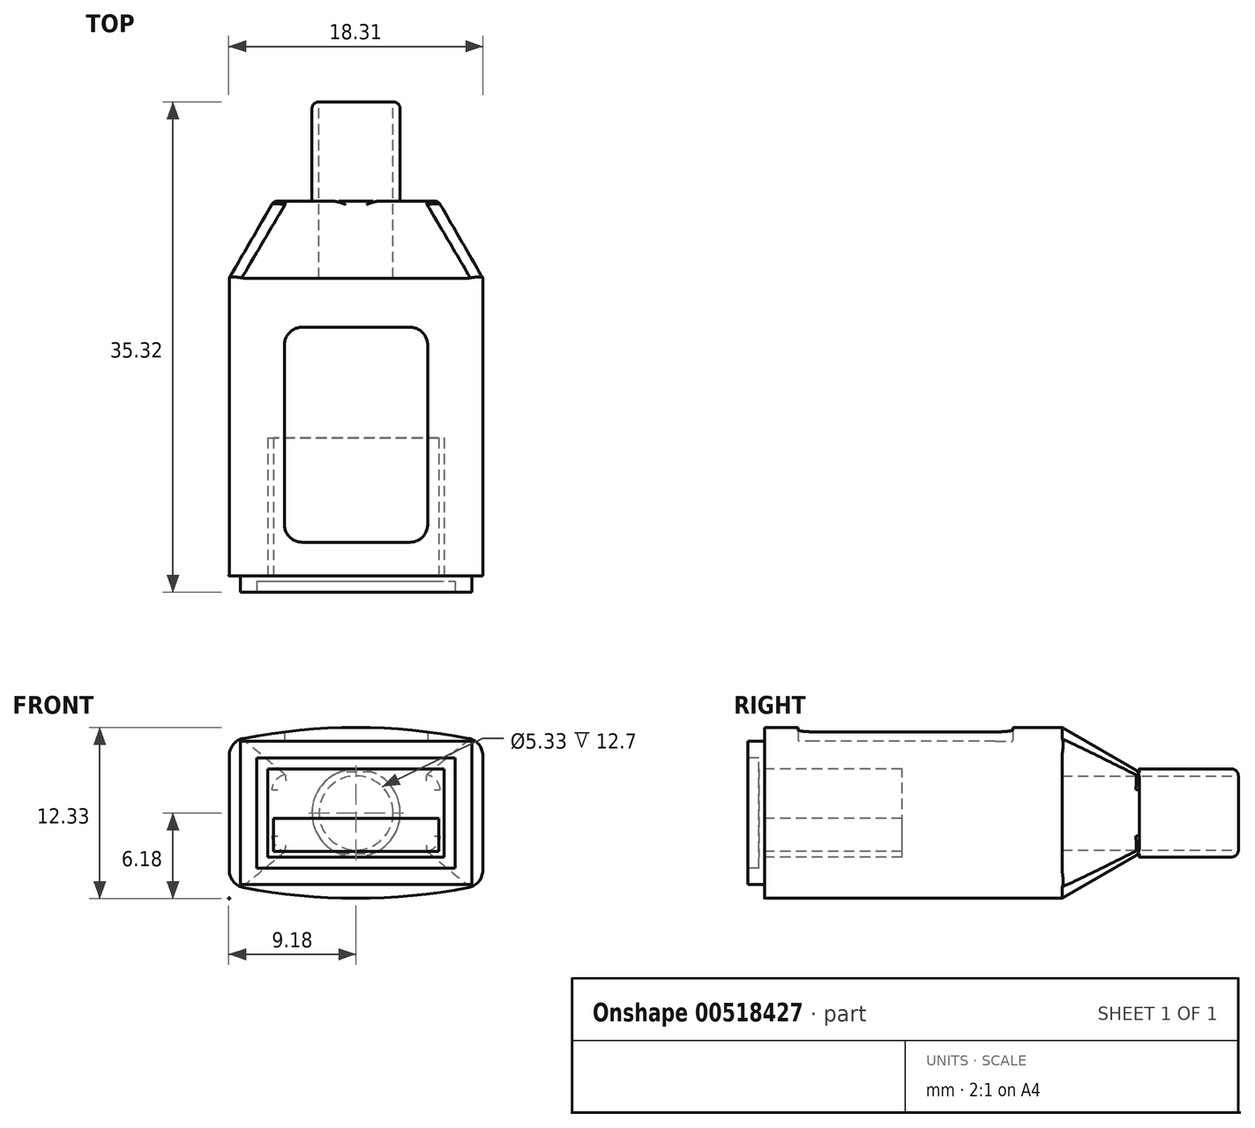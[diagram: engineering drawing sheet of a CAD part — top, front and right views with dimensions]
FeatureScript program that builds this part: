
annotation { "Feature Type Name" : "Feature", "Feature Type Description" : "" }
export const myFeature = defineFeature(function(context is Context, id is Id, definition is map)
    precondition{}
    {
        {
            var Q0;
            Q0=qCreatedBy(makeId("Front.planeOp"),FACE);
            var sketch = newSketch(context, id + "F0", { "sketchPlane" : qUnion([Q0])});
            skLineSegment(sketch, "E0.left", {"start": v(9.13, 0) * mm, "end": v(9.13, 5.16) * mm});
            skLineSegment(sketch, "E0.right", {"start": v(-9.13, 0) * mm, "end": v(-9.13, 5.16) * mm});
            skPoint(sketch, "E0.middle", {"position": v(0, 0) * mm});
            skArc(sketch, "E1", {"start": v(9.13, 5.16) * mm, "mid": v(0, 6.15) * mm, "end": v(-9.13, 5.16) * mm});
            skLineSegment(sketch, "E2", {"start": v(-9.13, 0) * mm, "end": v(9.13, 0) * mm, "construction": true});
            skArc(sketch, "E3.MirrorCS", {"start": v(9.13, -5.16) * mm, "mid": v(0, -6.15) * mm, "end": v(-9.13, -5.16) * mm});
            skLineSegment(sketch, "E4.MirrorCS", {"start": v(-9.13, 0) * mm, "end": v(-9.13, -5.16) * mm});
            skLineSegment(sketch, "E5.MirrorCS", {"start": v(9.13, 0) * mm, "end": v(9.13, -5.16) * mm});
            skSolve(sketch);
        }
        {
            var Q0;
            Q0 = qSketchRegion(id + "F0", true);
            extrude(context, id + "F1", {"entities" : qUnion([Q0]), "depth" : 21.43 * mm, "offsetDistance" : 25.4 * mm});
        }
        {
            var Q0;
            Q0=makeQuery(id+"F1.opExtrude","CAP_FACE",FACE,{"disambiguationData":[OSD([sQuery(id+"F0.wireOp",EDGE,"E0.left"),sQuery(id+"F0.wireOp",EDGE,"E0.right"),sQuery(id+"F0.wireOp",EDGE,"E1"),sQuery(id+"F0.wireOp",EDGE,"E3.MirrorCS"),sQuery(id+"F0.wireOp",EDGE,"E4.MirrorCS"),sQuery(id+"F0.wireOp",EDGE,"E5.MirrorCS")])],"isStart":false});
            var sketch = newSketch(context, id + "F2", { "sketchPlane" : qUnion([Q0])});
            skLineSegment(sketch, "E6.bottom", {"start": v(8.33, -5.16) * mm, "end": v(-8.33, -5.16) * mm});
            skLineSegment(sketch, "E6.top", {"start": v(8.33, 5.16) * mm, "end": v(-8.33, 5.16) * mm});
            skLineSegment(sketch, "E6.left", {"start": v(8.33, -5.16) * mm, "end": v(8.33, 5.16) * mm});
            skLineSegment(sketch, "E6.right", {"start": v(-8.33, -5.16) * mm, "end": v(-8.33, 5.16) * mm});
            skPoint(sketch, "E6.middle", {"position": v(0, 0) * mm});
            skSolve(sketch);
        }
        {
            var Q0;
            Q0 = qSketchRegion(id + "F2", true);
            extrude(context, id + "F3", {"entities" : qUnion([Q0]), "operationType" : NewBodyOperationType.ADD, "depth" : 1.2 * mm, "offsetDistance" : 25.4 * mm});
        }
        {
            var Q0;
            Q0=makeQuery(id+"F3.opExtrude","CAP_FACE",FACE,{"disambiguationData":[OSD([sQuery(id+"F2.wireOp",EDGE,"E6.bottom"),sQuery(id+"F2.wireOp",EDGE,"E6.top"),sQuery(id+"F2.wireOp",EDGE,"E6.left"),sQuery(id+"F2.wireOp",EDGE,"E6.right")])],"isStart":false});
            var sketch = newSketch(context, id + "F4", { "sketchPlane" : qUnion([Q0])});
            skLineSegment(sketch, "E7.0", {"start": v(7.14, -3.97) * mm, "end": v(7.14, 3.97) * mm});
            skLineSegment(sketch, "E7.1", {"start": v(-7.14, -3.97) * mm, "end": v(7.14, -3.97) * mm});
            skLineSegment(sketch, "E7.2", {"start": v(-7.14, 3.97) * mm, "end": v(-7.14, -3.97) * mm});
            skLineSegment(sketch, "E7.3", {"start": v(7.14, 3.97) * mm, "end": v(-7.14, 3.97) * mm});
            skSolve(sketch);
        }
        {
            var Q0;
            Q0 = qSketchRegion(id + "F4", true);
            extrude(context, id + "F5", {"entities" : qUnion([Q0]), "operationType" : NewBodyOperationType.REMOVE, "oppositeDirection" : true, "depth" : 0.8 * mm, "offsetDistance" : 25.4 * mm});
        }
        {
            var Q0;
            Q0=makeQuery(id+"F5.boolean.opBoolean","COPY",FACE,{"derivedFrom":makeQuery(id+"F5.opExtrude","CAP_FACE",FACE,{"disambiguationData":[OSD([sQuery(id+"F4.wireOp",EDGE,"E7.0"),sQuery(id+"F4.wireOp",EDGE,"E7.1"),sQuery(id+"F4.wireOp",EDGE,"E7.2"),sQuery(id+"F4.wireOp",EDGE,"E7.3")])],"isStart":false})});
            var sketch = newSketch(context, id + "F6", { "sketchPlane" : qUnion([Q0])});
            skLineSegment(sketch, "E8.0", {"start": v(6.35, -3.18) * mm, "end": v(6.35, 3.18) * mm});
            skLineSegment(sketch, "E8.1", {"start": v(-6.35, -3.18) * mm, "end": v(6.35, -3.18) * mm});
            skLineSegment(sketch, "E8.2", {"start": v(-6.35, 3.18) * mm, "end": v(-6.35, -3.18) * mm});
            skLineSegment(sketch, "E8.3", {"start": v(6.35, 3.18) * mm, "end": v(-6.35, 3.18) * mm});
            skSolve(sketch);
        }
        {
            var Q0;
            Q0 = qSketchRegion(id + "F6", true);
            extrude(context, id + "F7", {"entities" : qUnion([Q0]), "operationType" : NewBodyOperationType.REMOVE, "oppositeDirection" : true, "depth" : 10.32 * mm, "offsetDistance" : 25.4 * mm});
        }
        {
            var Q0;
            Q0=makeQuery(id+"F5.boolean.opBoolean","COPY",FACE,{"derivedFrom":makeQuery(id+"F5.opExtrude","CAP_FACE",FACE,{"disambiguationData":[OSD([sQuery(id+"F4.wireOp",EDGE,"E7.0"),sQuery(id+"F4.wireOp",EDGE,"E7.1"),sQuery(id+"F4.wireOp",EDGE,"E7.2"),sQuery(id+"F4.wireOp",EDGE,"E7.3")])],"isStart":false})});
            var sketch = newSketch(context, id + "F8", { "sketchPlane" : qUnion([Q0])});
            skLineSegment(sketch, "E9.0", {"start": v(5.95, -2.78) * mm, "end": v(5.95, -0.4) * mm});
            skLineSegment(sketch, "E9.1", {"start": v(-5.95, -2.78) * mm, "end": v(5.95, -2.78) * mm});
            skLineSegment(sketch, "E9.2", {"start": v(-5.95, -0.4) * mm, "end": v(-5.95, -2.78) * mm});
            skLineSegment(sketch, "E10", {"start": v(-5.95, -0.4) * mm, "end": v(5.95, -0.4) * mm});
            skSolve(sketch);
        }
        {
            var Q0;
            Q0 = qSketchRegion(id + "F8", true);
            var Q1;
            Q1=makeQuery(id+"F7.boolean.opBoolean","COPY",FACE,{"derivedFrom":makeQuery(id+"F7.opExtrude","CAP_FACE",FACE,{"disambiguationData":[OSD([sQuery(id+"F6.wireOp",EDGE,"E8.0"),sQuery(id+"F6.wireOp",EDGE,"E8.1"),sQuery(id+"F6.wireOp",EDGE,"E8.2"),sQuery(id+"F6.wireOp",EDGE,"E8.3")])],"isStart":false})});
            extrude(context, id + "F9", {"entities" : qUnion([Q0]), "operationType" : NewBodyOperationType.ADD, "endBound" : BoundingType.UP_TO_SURFACE, "oppositeDirection" : true, "depth" : 25.4 * mm, "endBoundEntityFace" : qUnion([Q1]), "offsetDistance" : 25.4 * mm});
        }
        {
            var Q0;
            Q0=makeQuery(id+"F3.opExtrude","SWEPT_FACE",FACE,{"disambiguationData":[OSD([sQuery(id+"F2.wireOp",EDGE,"E6.top")])]});
            var sketch = newSketch(context, id + "F10", { "sketchPlane" : qUnion([Q0])});
            skLineSegment(sketch, "E11.bottom", {"start": v(3.89, -3.54) * mm, "end": v(-3.89, -3.54) * mm});
            skLineSegment(sketch, "E11.top", {"start": v(3.89, -19.02) * mm, "end": v(-3.89, -19.02) * mm});
            skLineSegment(sketch, "E11.left", {"start": v(5.16, -4.8) * mm, "end": v(5.16, -17.75) * mm});
            skLineSegment(sketch, "E11.right", {"start": v(-5.16, -4.8) * mm, "end": v(-5.16, -17.75) * mm});
            skPoint(sketch, "E11.middle", {"position": v(0, -11.28) * mm});
            skPoint(sketch, "E12.visualSharp", {"position": v(-5.16, -19.02) * mm});
            skArc(sketch, "E12.filletArc", {"start": v(-5.16, -17.75) * mm, "mid": v(-4.79, -18.65) * mm, "end": v(-3.89, -19.02) * mm});
            skPoint(sketch, "E13.visualSharp", {"position": v(-5.16, -3.54) * mm});
            skArc(sketch, "E13.filletArc", {"start": v(-3.89, -3.54) * mm, "mid": v(-4.79, -3.91) * mm, "end": v(-5.16, -4.8) * mm});
            skPoint(sketch, "E14.visualSharp", {"position": v(5.16, -3.54) * mm});
            skArc(sketch, "E14.filletArc", {"start": v(5.16, -4.8) * mm, "mid": v(4.79, -3.91) * mm, "end": v(3.89, -3.54) * mm});
            skPoint(sketch, "E15.visualSharp", {"position": v(5.16, -19.02) * mm});
            skArc(sketch, "E15.filletArc", {"start": v(3.89, -19.02) * mm, "mid": v(4.79, -18.65) * mm, "end": v(5.16, -17.75) * mm});
            skSolve(sketch);
        }
        {
            var Q0;
            Q0 = qSketchRegion(id + "F10", true);
            var Q1;
            Q1=makeQuery(id+"F1.opExtrude","SWEPT_FACE",FACE,{"disambiguationData":[OSD([sQuery(id+"F0.wireOp",EDGE,"E1")])]});
            extrude(context, id + "F11", {"entities" : qUnion([Q0]), "operationType" : NewBodyOperationType.REMOVE, "endBound" : BoundingType.UP_TO_SURFACE, "depth" : 25.4 * mm, "endBoundEntityFace" : qUnion([Q1]), "offsetDistance" : 25.4 * mm});
        }
        {
            var Q0;
            Q0=makeQuery(id+"F1.opExtrude","CAP_FACE",FACE,{"disambiguationData":[OSD([sQuery(id+"F0.wireOp",EDGE,"E0.left"),sQuery(id+"F0.wireOp",EDGE,"E0.right"),sQuery(id+"F0.wireOp",EDGE,"E1"),sQuery(id+"F0.wireOp",EDGE,"E3.MirrorCS"),sQuery(id+"F0.wireOp",EDGE,"E4.MirrorCS"),sQuery(id+"F0.wireOp",EDGE,"E5.MirrorCS")])],"isStart":true});
            var sketch = newSketch(context, id + "F12", { "sketchPlane" : qUnion([Q0])});
            skLineSegment(sketch, "E16.0.0", {"start": v(9.13, -5.16) * mm, "end": v(9.13, 5.16) * mm});
            skArc(sketch, "E16.0.1", {"start": v(9.13, 5.16) * mm, "mid": v(0, 6.15) * mm, "end": v(-9.13, 5.16) * mm});
            skLineSegment(sketch, "E16.0.2", {"start": v(-9.13, 5.16) * mm, "end": v(-9.13, -5.16) * mm});
            skArc(sketch, "E16.0.3", {"start": v(-9.13, -5.16) * mm, "mid": v(0, -6.15) * mm, "end": v(9.13, -5.16) * mm});
            skSolve(sketch);
        }
        {
            var Q0;
            Q0 = qSketchRegion(id + "F12", true);
            extrude(context, id + "F13", {"entities" : qUnion([Q0]), "operationType" : NewBodyOperationType.ADD, "depth" : 5.56 * mm, "offsetDistance" : 25.4 * mm, "hasDraft" : true, "draftAngle" : 30 * degree, "draftPullDirection" : true});
        }
        {
            var Q0;
            Q0=makeQuery(id+"F13.opExtrude","CAP_FACE",FACE,{"disambiguationData":[OSD([sQuery(id+"F12.wireOp",EDGE,"E16.0.0"),sQuery(id+"F12.wireOp",EDGE,"E16.0.1"),sQuery(id+"F12.wireOp",EDGE,"E16.0.2"),sQuery(id+"F12.wireOp",EDGE,"E16.0.3")])],"isStart":false});
            var sketch = newSketch(context, id + "F14", { "sketchPlane" : qUnion([Q0])});
            skCircle(sketch, "E17", {"center": v(0, 0) * mm, "radius": 3.18 * mm});
            skSolve(sketch);
        }
        {
            var Q0;
            Q0 = qSketchRegion(id + "F14", true);
            extrude(context, id + "F15", {"entities" : qUnion([Q0]), "operationType" : NewBodyOperationType.ADD, "depth" : 7.14 * mm, "offsetDistance" : 25.4 * mm});
        }
        {
            var Q0;
            Q0=makeQuery(id+"F1.opExtrude","SWEPT_EDGE",EDGE,{"disambiguationData":[OSD([sQuery(id+"F0.wireOp",EDGE,"E0.left"),sQuery(id+"F0.wireOp",EDGE,"E1")])]});
            var Q1;
            Q1=makeQuery(id+"F1.opExtrude","SWEPT_EDGE",EDGE,{"disambiguationData":[OSD([sQuery(id+"F0.wireOp",EDGE,"E0.right"),sQuery(id+"F0.wireOp",EDGE,"E1")])]});
            var Q2;
            Q2=makeQuery(id+"F1.opExtrude","SWEPT_EDGE",EDGE,{"disambiguationData":[OSD([sQuery(id+"F0.wireOp",EDGE,"E3.MirrorCS"),sQuery(id+"F0.wireOp",EDGE,"E4.MirrorCS")])]});
            var Q3;
            Q3=makeQuery(id+"F1.opExtrude","SWEPT_EDGE",EDGE,{"disambiguationData":[OSD([sQuery(id+"F0.wireOp",EDGE,"E3.MirrorCS"),sQuery(id+"F0.wireOp",EDGE,"E5.MirrorCS")])]});
            fillet(context, id + "F16", {"entities" : qUnion([Q0, Q1, Q2, Q3]), "radius" : 1.27 * mm, "tangentPropagation" : true, "allowEdgeOverflow" : false});
        }
        {
            var Q0;
            Q0=makeQuery(id+"F13.opExtrude","SWEPT_EDGE",EDGE,{"disambiguationData":[OSD([sQuery(id+"F12.wireOp",EDGE,"E16.0.0"),sQuery(id+"F12.wireOp",EDGE,"E16.0.1")])]});
            var Q1;
            Q1=makeQuery(id+"F13.opExtrude","SWEPT_EDGE",EDGE,{"disambiguationData":[OSD([sQuery(id+"F12.wireOp",EDGE,"E16.0.1"),sQuery(id+"F12.wireOp",EDGE,"E16.0.2")])]});
            var Q2;
            Q2=makeQuery(id+"F13.opExtrude","SWEPT_EDGE",EDGE,{"disambiguationData":[OSD([sQuery(id+"F12.wireOp",EDGE,"E16.0.2"),sQuery(id+"F12.wireOp",EDGE,"E16.0.3")])]});
            var Q3;
            Q3=makeQuery(id+"F13.opExtrude","SWEPT_EDGE",EDGE,{"disambiguationData":[OSD([sQuery(id+"F12.wireOp",EDGE,"E16.0.0"),sQuery(id+"F12.wireOp",EDGE,"E16.0.3")])]});
            fillet(context, id + "F17", {"entities" : qUnion([Q0, Q1, Q2, Q3]), "radius" : 1.27 * mm, "tangentPropagation" : true, "allowEdgeOverflow" : false});
        }
        {
            var Q0;
            {var subQ0=sQuery(id+"F12.wireOp",EDGE,"E16.0.1");var subQ1=makeQuery(id+"F13.opExtrude","SWEPT_FACE",FACE,{"disambiguationData":[OSD([subQ0])]});var subQ3=sQuery(id+"F12.wireOp",EDGE,"E16.0.0");var subQ4=makeQuery(id+"F13.opExtrude","CAP_FACE",FACE,{"disambiguationData":[OSD([subQ3,subQ0,sQuery(id+"F12.wireOp",EDGE,"E16.0.2"),sQuery(id+"F12.wireOp",EDGE,"E16.0.3")])],"isStart":false});Q0=makeQuery(id+"F15.boolean.opBoolean","SPLIT",EDGE,{"disambiguationData":[topologyDisambiguationEdgeConnected([subQ4,subQ1]),TD([makeQuery(id+"F13.opExtrude","SWEPT_FACE",FACE,{"disambiguationData":[OSD([subQ3])]})])],"derivedFrom":makeQuery(id+"F13.opExtrude","CAP_EDGE",EDGE,{"disambiguationData":[OSD([subQ0])],"isStart":false})});}
            var Q1;
            {var subQ0=sQuery(id+"F12.wireOp",EDGE,"E16.0.2");var subQ1=sQuery(id+"F12.wireOp",EDGE,"E16.0.1");var subQ2=makeQuery(id+"F13.opExtrude","SWEPT_FACE",FACE,{"disambiguationData":[OSD([subQ1])]});var subQ4=makeQuery(id+"F13.opExtrude","CAP_FACE",FACE,{"disambiguationData":[OSD([sQuery(id+"F12.wireOp",EDGE,"E16.0.0"),subQ1,subQ0,sQuery(id+"F12.wireOp",EDGE,"E16.0.3")])],"isStart":false});Q1=makeQuery(id+"F15.boolean.opBoolean","SPLIT",EDGE,{"disambiguationData":[topologyDisambiguationEdgeConnected([subQ4,subQ2]),TD([makeQuery(id+"F13.opExtrude","SWEPT_FACE",FACE,{"disambiguationData":[OSD([subQ0])]})])],"derivedFrom":makeQuery(id+"F13.opExtrude","CAP_EDGE",EDGE,{"disambiguationData":[OSD([subQ1])],"isStart":false})});}
            var Q2;
            Q2=makeQuery(id+"F15.opExtrude","CAP_EDGE",EDGE,{"disambiguationData":[OSD([sQuery(id+"F14.wireOp",EDGE,"E17")])],"isStart":false});
            fillet(context, id + "F18", {"entities" : qUnion([Q0, Q1, Q2]), "radius" : 0.5 * mm, "tangentPropagation" : true, "allowEdgeOverflow" : false});
        }
        {
            var Q0;
            Q0=makeQuery(id+"F15.opExtrude","CAP_FACE",FACE,{"disambiguationData":[OSD([sQuery(id+"F14.wireOp",EDGE,"E17")])],"isStart":false});
            var sketch = newSketch(context, id + "F19", { "sketchPlane" : qUnion([Q0])});
            skCircle(sketch, "E18.0.0", {"center": v(0, 0) * mm, "radius": 2.67 * mm});
            skSolve(sketch);
        }
        {
            var Q0;
            Q0 = qSketchRegion(id + "F19", true);
            extrude(context, id + "F20", {"entities" : qUnion([Q0]), "operationType" : NewBodyOperationType.REMOVE, "oppositeDirection" : true, "depth" : 12.7 * mm, "offsetDistance" : 25.4 * mm});
        }
        {
            var Q0;
            Q0=makeQuery(id+"F1.opExtrude","CAP_FACE",FACE,{"disambiguationData":[OSD([sQuery(id+"F0.wireOp",EDGE,"E0.left"),sQuery(id+"F0.wireOp",EDGE,"E0.right"),sQuery(id+"F0.wireOp",EDGE,"E1"),sQuery(id+"F0.wireOp",EDGE,"E3.MirrorCS"),sQuery(id+"F0.wireOp",EDGE,"E4.MirrorCS"),sQuery(id+"F0.wireOp",EDGE,"E5.MirrorCS")])],"isStart":false});
            var sketch = newSketch(context, id + "F21", { "sketchPlane" : qUnion([Q0])});
            skLineSegment(sketch, "E19", {"start": v(-9.13, -4.13) * mm, "end": v(-9.13, -6.15) * mm, "construction": true});
            skPoint(sketch, "E19.endSnap0", {"position": v(0, -6.15) * mm});
            skLineSegment(sketch, "E20", {"start": v(-9.13, -6.15) * mm, "end": v(0, -6.15) * mm, "construction": true});
            skLineSegment(sketch, "E21", {"start": v(-9.13, -4.13) * mm, "end": v(0, -6.15) * mm, "construction": true});
            skLineSegment(sketch, "E22.bottom", {"start": v(-9.08, -6.18) * mm, "end": v(-9.18, -6.18) * mm});
            skLineSegment(sketch, "E22.top", {"start": v(-9.08, -6.12) * mm, "end": v(-9.18, -6.12) * mm});
            skLineSegment(sketch, "E22.left", {"start": v(-9.08, -6.18) * mm, "end": v(-9.08, -6.12) * mm});
            skLineSegment(sketch, "E22.right", {"start": v(-9.18, -6.18) * mm, "end": v(-9.18, -6.12) * mm});
            skPoint(sketch, "E22.middle", {"position": v(-9.13, -6.15) * mm});
            skSolve(sketch);
        }
        {
            var Q0;
            Q0 = qSketchRegion(id + "F21", true);
            var Q1;
            Q1 = qConstructionFilter(qBodyType(qCreatedBy(id + "F21" ,EDGE), BodyType.WIRE), ConstructionObject.NO);
            extrude(context, id + "F22", {"entities" : qUnion([Q0]), "surfaceEntities" : qUnion([Q1]), "oppositeDirection" : true, "depth" : 0.03 * mm, "offsetDistance" : 25.4 * mm});
        }
    });
